# Revit family: ledlinear-e2_l12-22_36w-830_840_531000019000_056b
name_source: partatom
category: Lighting Fixtures
units: mm (PartAtom-declared; Revit-internal decimal feet)

## family parameters
Cut with Voids When Loaded = No
Host = Face
Light Source = No
Part Type = Normal
Room Calculation Point = No
Round Connector Dimension = Use Diameter
Shared = No

## types (1)
- LEDLinear-E2 L12-22/36W-830/840 (1 x LED, 4680 lm, 4000)
    Apparent Load = 22 VA
    Approval mark = CE
    CIE Flux Codes = 44 74 92 95 100
    Color Rendering = 80
    Color Temperature = 4000
    Control Gear = Electronic ballast
    Default Elevation = 1800 mm
    Description = Linear EcoMax G2 1200mm-36W-2860/4680lm-3/4000K
    Frequency = 60 Hz
    Height = 75 mm
    Lamp = 1 x LED
    Lamp Light Flux = 4680 lm
    Lamp count = 1
    Length = 1200 mm
    Luminous efficacy = 213 lm/W
    Manufacturer = OPPLE
    ModVariant = No
    Model = 531000019000
    Mounting Place = Ceiling
    Mounting Type = Surface mounted
    Number of Poles = 1
    OnlyDefault = Yes
    Power Factor = 1
    Product Name = LEDLinear-E2 L12-22/36W-830/840
    Product group = Ceiling mounted luminaire
    ProductGroupID = 3
    Protection Class = Protection class I
    Protection Degree = IP 44
    RLX_Detail_Level = 1
    RLX_Emergency_Light_Flux = 0 lm
    RLX_Emergency_Type = 0
    RLX_Emergency_Type_DB = No
    RlxData = <blob elided: 95525 chars, md5=e09a45e6>
    Socket = socket
    Standby Power = 0 W
    System Light Flux = 4680 lm
    System Power = 22 W
    Type Comments = Product without accessories
    Type Image = web_linear_e2_l12_l15.jpg
    URL = http://relux.com
    VarID = ---
    Voltage = 230 V
    Voltage Range = 220-240 V
    Weight = 0.00 kg
    Width = 180 mm  [stored 0.590551 ft]

note: [stored X ft] marks values corroborated as IEEE doubles in the binary element streams (Revit-internal decimal feet)

## geometry (parser evidence)
native form markers: Blend x4, Sweep x13
no freeform markers — native parametric forms only
